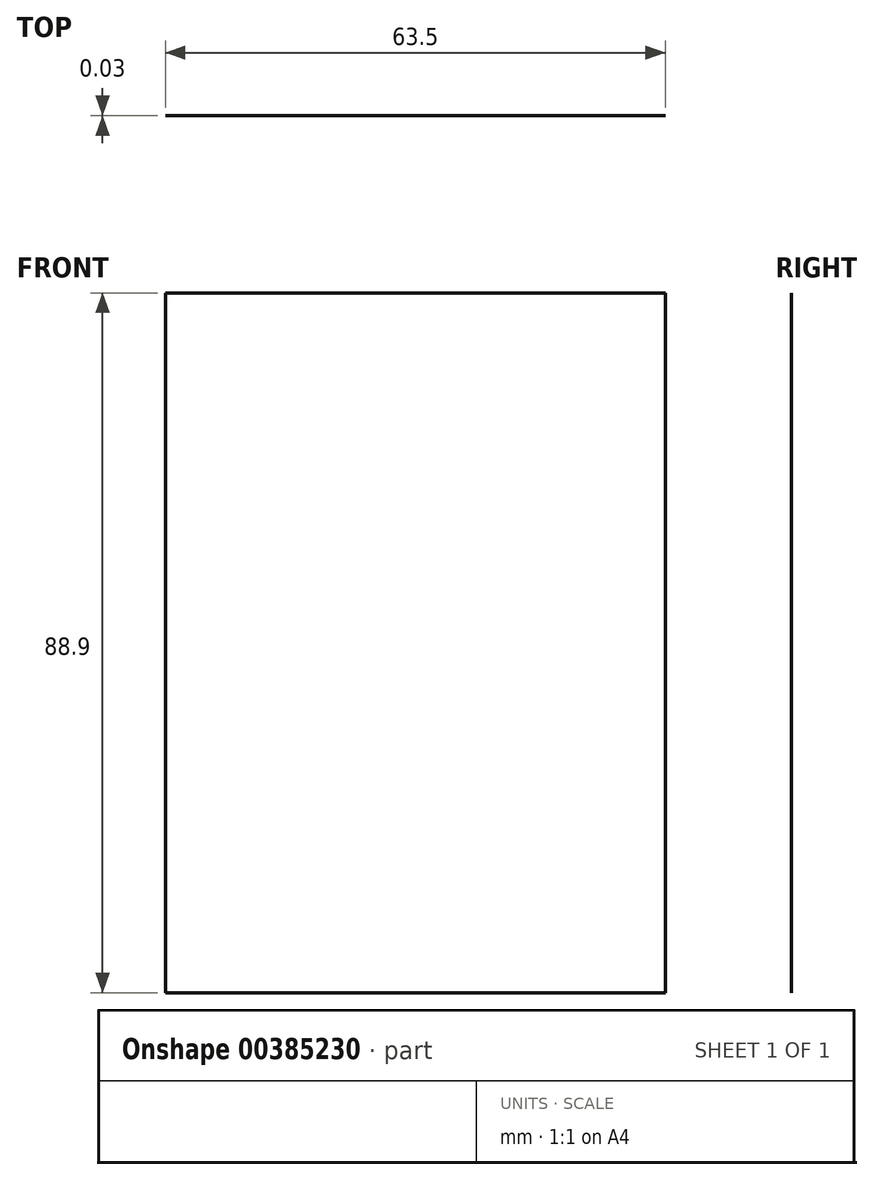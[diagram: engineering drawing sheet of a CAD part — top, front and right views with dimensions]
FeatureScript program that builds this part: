
annotation { "Feature Type Name" : "Feature", "Feature Type Description" : "" }
export const myFeature = defineFeature(function(context is Context, id is Id, definition is map)
    precondition{}
    {
        {
            var Q0;
            Q0=qCreatedBy(makeId("Front.planeOp"),FACE);
            var sketch = newSketch(context, id + "F0", { "sketchPlane" : qUnion([Q0])});
            skLineSegment(sketch, "E0.bottom", {"start": v(0, 0) * mm, "end": v(63.5, 0) * mm});
            skLineSegment(sketch, "E0.top", {"start": v(0, 88.9) * mm, "end": v(63.5, 88.9) * mm});
            skLineSegment(sketch, "E0.left", {"start": v(0, 0) * mm, "end": v(0, 88.9) * mm});
            skLineSegment(sketch, "E0.right", {"start": v(63.5, 0) * mm, "end": v(63.5, 88.9) * mm});
            skSolve(sketch);
        }
        {
            var Q0;
            Q0 = qSketchRegion(id + "F0", true);
            extrude(context, id + "F1", {"entities" : qUnion([Q0]), "depth" : 3 / 101.6 * mm});
        }
    });
